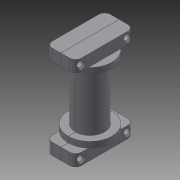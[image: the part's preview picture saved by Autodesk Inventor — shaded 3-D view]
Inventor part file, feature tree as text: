
AUTODESK INVENTOR PART (.ipt)
format: ipt  version: 2015 (Build 190159000, 159)  size: 231,936 bytes
history: native  units: mm
features: sketch x9, extrude x7, hole x2, fillet x1
ambient origin geometry x8: Origin, YZ Plane, XZ Plane, XY Plane, X Axis, Y Axis, Z Axis, Center Point
bodies: Solid1 (feature_tree)
feature tree (19):
  extrude  "Extrusion1"  Depth=10.0mm
  extrude  "Extrusion2"  Depth=15.0mm
  extrude  "Extrusion3"  Depth=2.0mm TaperAngle=0.0deg
  extrude  "Extrusion4"  Depth=10.0mm
  extrude  "Extrusion5"  Depth=7.5mm
  hole  "Hole1"  [1 undecoded]
  extrude  "Extrusion6"  Depth=4.0mm TaperAngle=0.0deg
  hole  "Hole2"  [1 undecoded]
  fillet  "Fillet1"  Radius=2.0mm
  extrude  "Extrusion7"  Depth=2.0mm TaperAngle=0.0deg
  sketch  "Sketch1"  dims[d0=5.5mm d1=10.0mm]
  sketch  "Sketch2"  dims[d2=20.0mm d3=0.0mm d4=15.0mm]
  sketch  "Sketch3"  dims[d5=2.0mm d6=0.0mm d7=2.0mm d8=0.0mm]
  sketch  "Sketch4"  dims[d9=10.0mm d10=10.0mm]
  sketch  "Sketch5"  dims[d11=7.5mm d12=7.5mm]
  sketch  "Sketch6"  dims[d13=4.0mm d14=0.0mm d15=10.0mm]
  sketch  "Sketch7"  dims[d16=2.5mm d17=4.0mm d18=0.0mm]
  sketch  "Sketch8"  dims[d19=2.0mm d20=2.0mm d21=2.0mm]
  sketch  "Sketch9"  dims[d22=2.0mm d23=2.0mm d24=6.0mm d25=3.0mm d26=2.0mm d27=90.0deg d28=10.0mm d29=20.594885mm d30=4.0mm d31=0.0mm d32=2.0mm d33=2.0mm d34=2.0mm d35=6.0mm d36=3.0mm d37=2.0mm d38=90.0deg d39=10.0mm d40=20.594885mm d41=2.0mm d42=0.01mm d43=0.01mm d44=50.0mm d45=0.0mm]
note: 2 required parameter values undecoded (feature->parameter linkage not recoverable at this tier; creation-order binding heuristic only, values carry confidence <= 0.55)
